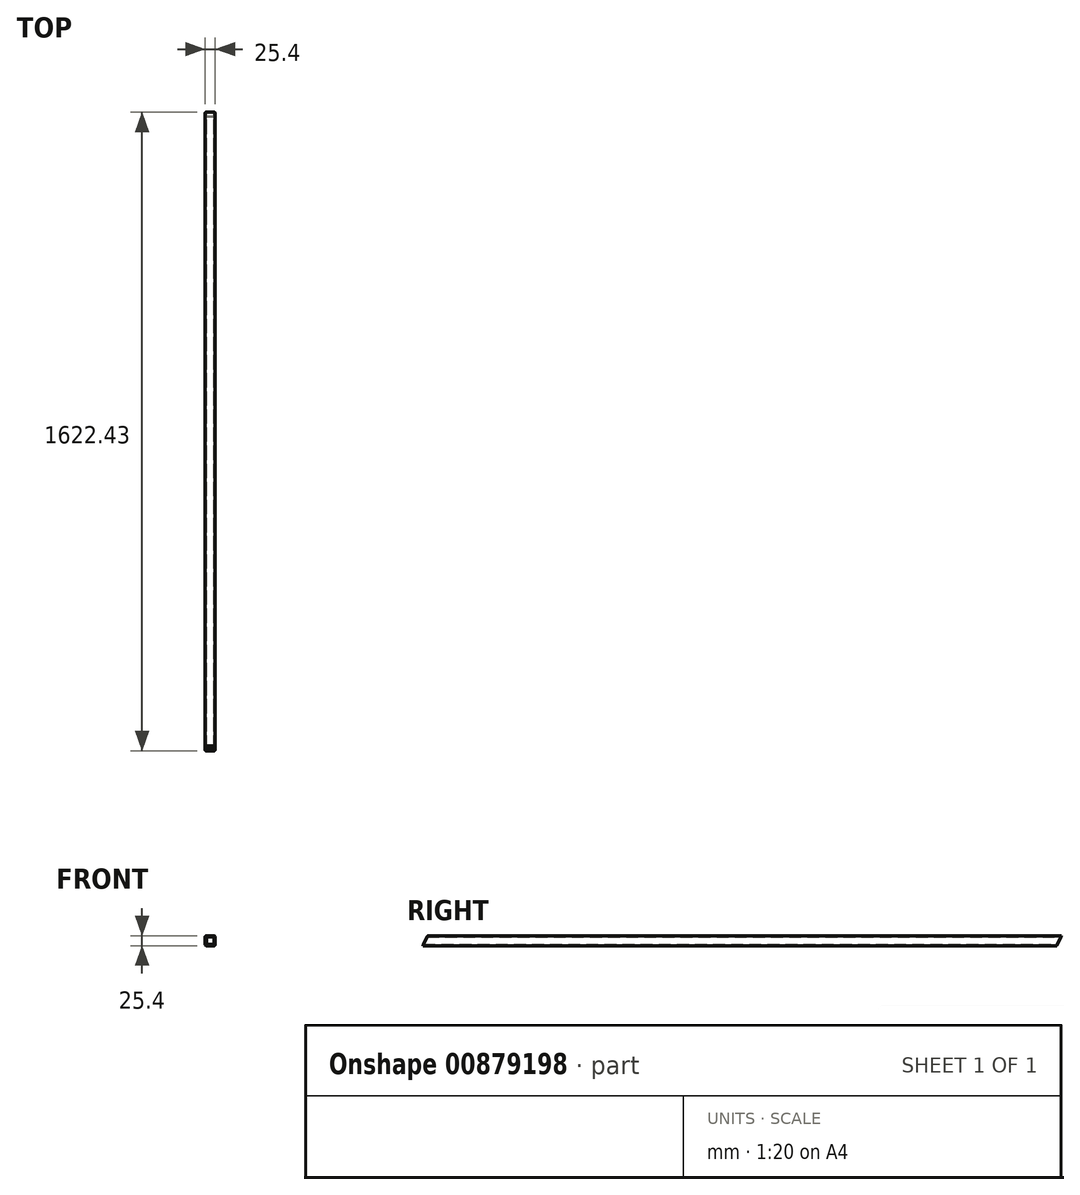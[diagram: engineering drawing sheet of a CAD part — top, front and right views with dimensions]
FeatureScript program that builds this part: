
annotation { "Feature Type Name" : "Feature", "Feature Type Description" : "" }
export const myFeature = defineFeature(function(context is Context, id is Id, definition is map)
    precondition{}
    {
        {
            var Q0;
            Q0=qCreatedBy(makeId("Front.planeOp"),FACE);
            var sketch = newSketch(context, id + "F0", { "sketchPlane" : qUnion([Q0])});
            skLineSegment(sketch, "E0.bottom", {"start": v(8.82, -12.02) * mm, "end": v(-10.23, -12.02) * mm});
            skLineSegment(sketch, "E0.top", {"start": v(8.82, 13.38) * mm, "end": v(-10.23, 13.38) * mm});
            skLineSegment(sketch, "E0.left", {"start": v(12, -8.85) * mm, "end": v(12, 10.2) * mm});
            skLineSegment(sketch, "E0.right", {"start": v(-13.4, -8.85) * mm, "end": v(-13.4, 10.2) * mm});
            skLineSegment(sketch, "E1.bottom", {"start": v(5.65, -8.85) * mm, "end": v(-7.05, -8.85) * mm});
            skLineSegment(sketch, "E1.top", {"start": v(5.65, 10.2) * mm, "end": v(-7.05, 10.2) * mm});
            skLineSegment(sketch, "E1.left", {"start": v(8.82, -5.67) * mm, "end": v(8.82, 7.03) * mm});
            skLineSegment(sketch, "E1.right", {"start": v(-10.23, -5.67) * mm, "end": v(-10.23, 7.03) * mm});
            skPoint(sketch, "E2.visualSharp", {"position": v(8.82, 10.2) * mm});
            skArc(sketch, "E2.filletArc", {"start": v(8.82, 7.03) * mm, "mid": v(7.9, 9.27) * mm, "end": v(5.65, 10.2) * mm});
            skPoint(sketch, "E3.visualSharp", {"position": v(-10.23, 10.2) * mm});
            skArc(sketch, "E3.filletArc", {"start": v(-7.05, 10.2) * mm, "mid": v(-9.3, 9.27) * mm, "end": v(-10.23, 7.03) * mm});
            skPoint(sketch, "E4.visualSharp", {"position": v(-10.23, -8.85) * mm});
            skArc(sketch, "E4.filletArc", {"start": v(-10.23, -5.67) * mm, "mid": v(-9.3, -7.92) * mm, "end": v(-7.05, -8.85) * mm});
            skPoint(sketch, "E5.visualSharp", {"position": v(8.82, -8.85) * mm});
            skArc(sketch, "E5.filletArc", {"start": v(5.65, -8.85) * mm, "mid": v(7.9, -7.92) * mm, "end": v(8.82, -5.67) * mm});
            skPoint(sketch, "E6.visualSharp", {"position": v(12, 13.38) * mm});
            skArc(sketch, "E6.filletArc", {"start": v(12, 10.2) * mm, "mid": v(11.07, 12.45) * mm, "end": v(8.82, 13.38) * mm});
            skPoint(sketch, "E7.visualSharp", {"position": v(-13.4, 13.38) * mm});
            skArc(sketch, "E7.filletArc", {"start": v(-10.23, 13.38) * mm, "mid": v(-12.47, 12.45) * mm, "end": v(-13.4, 10.2) * mm});
            skPoint(sketch, "E8.visualSharp", {"position": v(-13.4, -12.02) * mm});
            skArc(sketch, "E8.filletArc", {"start": v(-13.4, -8.85) * mm, "mid": v(-12.47, -11.1) * mm, "end": v(-10.23, -12.02) * mm});
            skPoint(sketch, "E9.visualSharp", {"position": v(12, -12.02) * mm});
            skArc(sketch, "E9.filletArc", {"start": v(8.82, -12.02) * mm, "mid": v(11.07, -11.1) * mm, "end": v(12, -8.85) * mm});
            skSolve(sketch);
        }
        {
            var Q0;
            Q0=qSketchRegion(id+"F0",true);
            extrude(context, id + "F1", {"entities" : qUnion([Q0]), "depth" : 1622.42 * mm, "offsetDistance" : 25.4 * mm});
        }
        {
            var Q0;
            Q0=qCreatedBy(makeId("Right.planeOp"),FACE);
            var sketch = newSketch(context, id + "F2", { "sketchPlane" : qUnion([Q0])});
            skLineSegment(sketch, "E10", {"start": v(0, 13.38) * mm, "end": v(0, -13.51) * mm});
            skLineSegment(sketch, "E11", {"start": v(-12.97, -13.51) * mm, "end": v(0, 13.38) * mm});
            skLineSegment(sketch, "E12", {"start": v(0, -13.51) * mm, "end": v(-12.97, -13.51) * mm});
            skSolve(sketch);
        }
        {
            var Q0;
            Q0=qSketchRegion(id+"F2",true);
            extrude(context, id + "F3", {"entities" : qUnion([Q0]), "operationType" : NewBodyOperationType.REMOVE, "endBound" : BoundingType.SYMMETRIC, "depth" : 76.2 * mm, "offsetDistance" : 25.4 * mm});
        }
        {
            var Q0;
            Q0=qCreatedBy(makeId("Right.planeOp"),FACE);
            var sketch = newSketch(context, id + "F4", { "sketchPlane" : qUnion([Q0])});
            skLineSegment(sketch, "E13", {"start": v(-1622.43, -12.02) * mm, "end": v(-1609.46, 14.86) * mm});
            skLineSegment(sketch, "E14", {"start": v(-1622.43, -12.02) * mm, "end": v(-1622.43, 14.86) * mm});
            skLineSegment(sketch, "E15", {"start": v(-1622.43, 14.86) * mm, "end": v(-1609.46, 14.86) * mm});
            skSolve(sketch);
        }
        {
            var Q0;
            Q0=qSketchRegion(id+"F4",true);
            extrude(context, id + "F5", {"entities" : qUnion([Q0]), "operationType" : NewBodyOperationType.REMOVE, "endBound" : BoundingType.SYMMETRIC, "depth" : 50.8 * mm, "offsetDistance" : 25.4 * mm});
        }
    });
